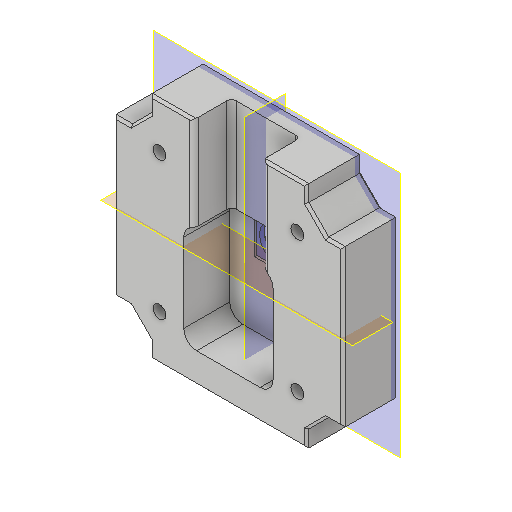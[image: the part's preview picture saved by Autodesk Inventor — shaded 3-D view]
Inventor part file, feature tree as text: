
AUTODESK INVENTOR PART (.ipt)
format: ipt  version: 2022 (Build 260153000, 153)  size: 384,000 bytes
history: native  units: mm
features: reference x17, other x10, sketch x7, extrude x6, plane x5, projected_geometry x3, chamfer x1, fillet x1, hole x1
ambient origin geometry x8: Origin, YZ Plane, XZ Plane, XY Plane, X Axis, Y Axis, Z Axis, Center Point
bodies: Solid1 (feature_tree)
feature tree (51):
  plane  "Work Plane1"
  extrude  "Extrusion1"  Depth=12.0mm
  extrude  "IM_offset"  Depth=53.8mm
  plane  "Arbeitsebene5"
  plane  "Arbeitsebene6"
  extrude  "Extrusion26"  Depth=45.0mm
  chamfer  "Fase2"  Distance=2.8mm
  plane  "Arbeitsebene9"
  extrude  "Extrusion29"  Depth=1.0mm
  extrude  "Extrusion30"  Depth=1.0mm
  sketch  "Skizze36"  dims[d32=2.8mm]
  plane  "Arbeitsebene10"
  extrude  "Extrusion31"  Depth=1.0mm
  fillet  "Rundung3"  Radius=0.1mm
  hole  "Bohrung2"  [1 undecoded]
  sketch  "Sketch1"  dims[d10=12.0mm d11=0.0mm d18=53.8mm]
  reference  "Reference1"
  reference  "Reference2"
  reference  "Reference3"
  reference  "Reference4"
  reference  "Reference9"
  reference  "Reference20"
  reference  "Reference21"
  reference  "Reference22"
  reference  "Reference23"
  reference  "Reference24"
  sketch  "Skizze4"  dims[d19=45.0deg d20=53.8mm]
  projected_geometry  "Projizierte Kontur1"
  sketch  "Skizze31"  dims[d21=45.0mm d22=45.0mm]
  projected_geometry  "Projizierte Kontur17"
  sketch  "Skizze34"  dims[d30=20.0mm]
  reference  "Referenz35"
  sketch  "Skizze35"  dims[d31=20.0mm]
  reference  "Referenz36"
  reference  "Referenz37"
  reference  "Referenz38"
  reference  "Referenz39"
  reference  "Referenz40"
  sketch  "Skizze37"  dims[d33=2.8mm d34=2.8mm d35=3.0mm d36=0.1mm d37=0.1mm d38=0.1mm d39=0.1mm d40=0.2mm d41=10.0mm d42=0.0mm d181=7.5mm d182=10.0mm d183=0.0mm d184=0.5mm d185=2.0mm d186=45.0deg d193=-1.5mm d194=8.6mm d195=8.6mm d196=0.0mm d197=0.0mm d198=10.0mm d199=0.0mm d200=4.0mm d201=12.0mm d202=0.0mm d203=1.0mm d204=30.0mm d205=30.0mm d206=2.8mm d207=6.0mm d208=8.0mm d209=6.0mm d210=90.0deg d211=8.0mm d212=20.594885mm d160=0.5mm d161=0.872665mm d162=0.5mm d163=0.872665mm]
  projected_geometry  "Projizierte Kontur18"
  reference  "Referenz41"
  other  "Assembly_Cube_v2_Thorlabs.iam"
  other  "10_Cube_Base:1"
  other  "00_Base_v0:1"
  other  "Assembly_Cube_Kinematic_Mirrormount_v2.iam"
  other  "Assembly_Cube_empty_1x1_v2:1"
  other  "10_Cube_1x1_v2:1"
  other  "10_Lid_1x1_v2:1"
  other  "Assembly_Cube_SEEED_Xiao_Sense_Camera_v3.iam"
  other  "00_Seeeduino Xiao:1"
  other  "10_Cube_Lid:1"
note: 1 required parameter value undecoded (feature->parameter linkage not recoverable at this tier; creation-order binding heuristic only, values carry confidence <= 0.55)
